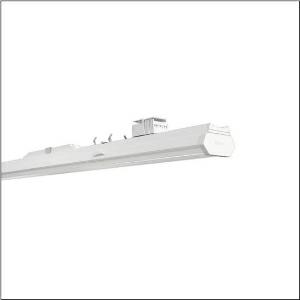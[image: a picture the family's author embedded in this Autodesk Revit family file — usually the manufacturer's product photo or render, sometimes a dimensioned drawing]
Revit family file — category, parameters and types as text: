
# Revit family: licross_21_protected_ho_52td13cn4c5s
name_source: partatom
category: Lighting Fixtures
units: mm (PartAtom-declared; Revit-internal decimal feet)

## family parameters
Cut with Voids When Loaded = No
Host = Face
Light Source = No
Part Type = Normal
Room Calculation Point = No
Round Connector Dimension = Use Diameter
Shared = No

## types (1)
- --- (1 x LED, 12680 lm, 68.9 W, 4000K)
    Apparent Load = 69 VA
    CIE Flux Codes = 89 96 99 100 99
    Color Rendering = 80
    Color Temperature = 4000K
    Default Elevation = 1800 mm
    Description = Licross 21 Protected HO, luminaire insert, of sheet steel, galvanised, coil coated, white, length: 1.500mm, width: 66mm, height: 67mm, LED rated luminous flux: 12.690lm, light colour: 840, SDCM (Standard Deviation of Colour Matching)MacAdam ≤ 3 SDCM (initial), control gear: ON/OFF Multilumen, CLOi, with plug, 3-pole, with phase selection, mains connection: 220..240V, AC, 50/60Hz, start of lifetime: 69W, end of service life: 83W, internal wiring halogen-free, primary light control with lens, of plastic, primary optical cover: cover, of PMMA, light emission: direct distribution, primary light characteristic: symmetric, protection rating (complete): IP54, insulation class (complete): insulation class I (protective earthing), certification: CE, ENEC, VDE, UKCA, protection symbol: D if used in an environment with non-conductive dust loads with corresponding accessories, impact resistance: IK06, permissible ambient temperature for indoor applications: -35..+35°C, corresponds to IFS (International Featured Standards) requirements for safety and quality in the food industry, reducing of maximum allowable ambient temperature of 5°C with ceiling mounting, LABS conformity tested according to VDMA 24364:2018-05, The light source and the operating device comply with the requirements of the Ecodesign Regulation (EU) 2019/2020 and are replaceable in accordance with this regulation, packaging unit: 1 piece
    Height = 92 mm
    Lamp = 1 x LED
    Lamp Light Flux = 12680 lm
    Lamp Power = 68.9 W
    Lamp count = 1
    Length = 1500 mm
    Luminous efficacy = 184 lm/W
    Manufacturer = Siteco
    ModVariant = No
    Model = 52TD13CN4C5S
    Mounting Place = Ceiling
    Mounting Type = Pendant
    Number of Poles = 1
    OnlyDefault = Yes
    Power Factor = 1
    Product Name = Licross 21 Protected HO
    Product group = luminaire insert | ceiling pendant
    ProductGroupID = 901
    Protection Class = Protection class I
    Protection Degree = IP 54
    RLX_Detail_Level = 1
    RLX_Emergency_Light_Flux = 0 lm
    RLX_Emergency_Type = 0
    RLX_Emergency_Type_DB = No
    RlxData = <blob elided: 22297 chars, md5=ce9ad701>
    Socket = socket
    Standby Power = 0 W
    System Light Flux = 12680 lm
    System Power = 69 W
    Type Comments = factory setting: luminous flux: 100 % | (A | C | E) | 162 mA
    Type Image = l_1256148.jpg
    URL = http://relux.com
    VarID = @adj_110793
    Voltage = 0 V
    Weight = 0.00 kg
    Width = 88 mm

## geometry (parser evidence)
native form markers: Blend x4, Sweep x13
no freeform markers — native parametric forms only
